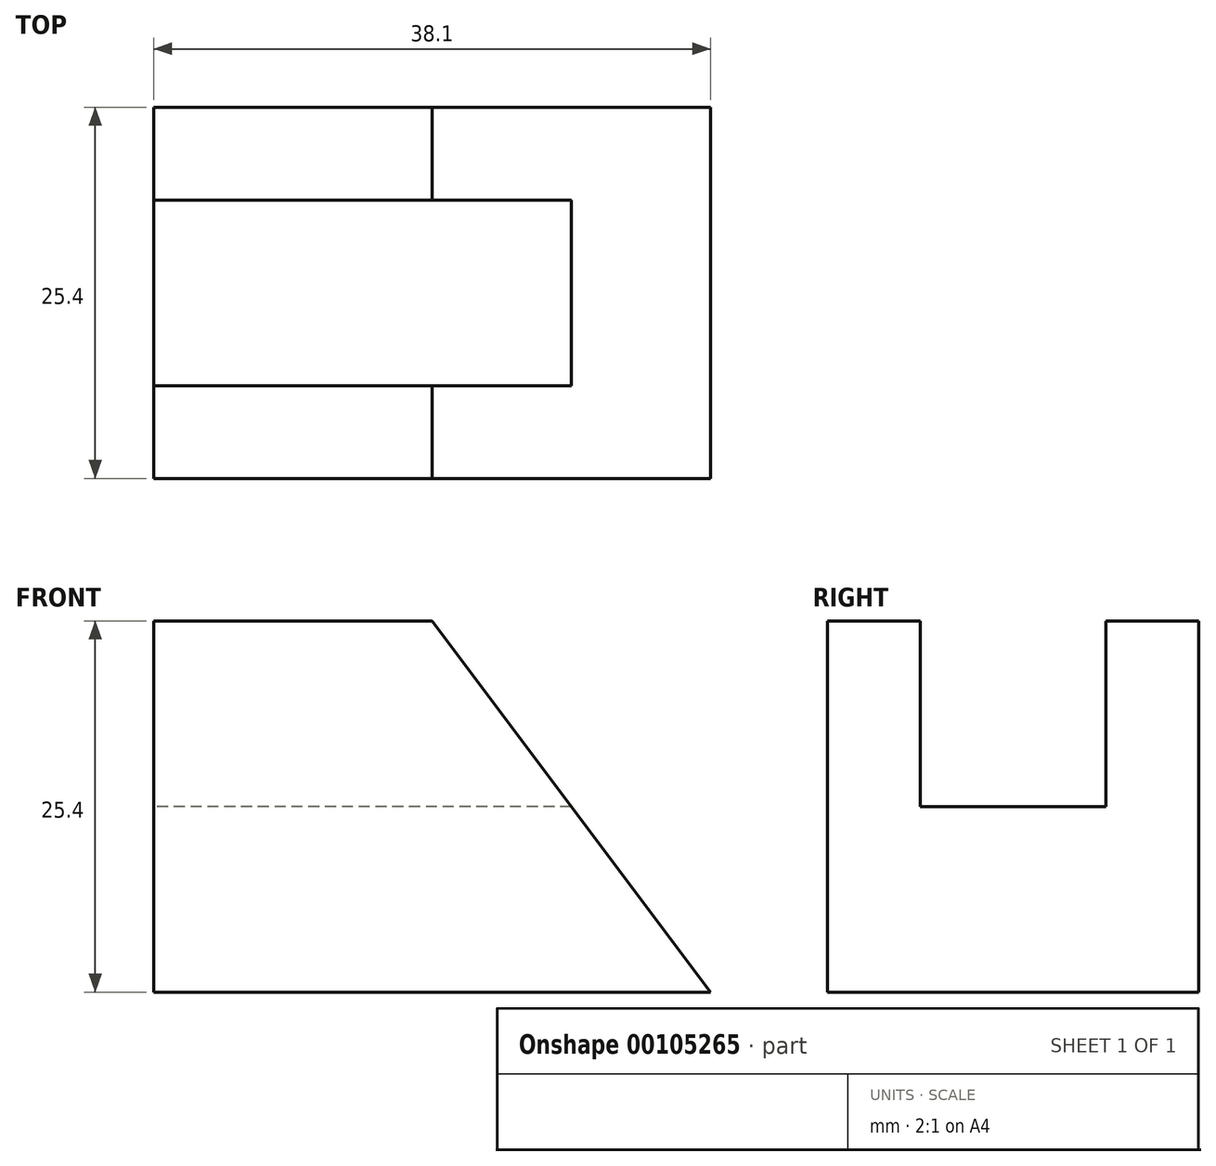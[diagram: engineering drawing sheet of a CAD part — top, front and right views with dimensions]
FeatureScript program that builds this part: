
annotation { "Feature Type Name" : "Feature", "Feature Type Description" : "" }
export const myFeature = defineFeature(function(context is Context, id is Id, definition is map)
    precondition{}
    {
        {
            var Q0;
            Q0=qCreatedBy(makeId("Front.planeOp"),FACE);
            var sketch = newSketch(context, id + "F0", { "sketchPlane" : qUnion([Q0])});
            skLineSegment(sketch, "E0.top", {"start": v(0, 25.4) * mm, "end": v(19.05, 25.4) * mm});
            skLineSegment(sketch, "E0.left", {"start": v(0, 0) * mm, "end": v(0, 25.4) * mm});
            skLineSegment(sketch, "E1", {"start": v(19.05, 25.4) * mm, "end": v(38.1, 0) * mm});
            skLineSegment(sketch, "E2", {"start": v(0, 0) * mm, "end": v(38.1, 0) * mm});
            skSolve(sketch);
        }
        {
            var Q0;
            Q0=makeQuery(id+"F0.imprint","IMPRINT",FACE,{"disambiguationData":[TD([[makeQuery(id+"F0.imprint","IMPRINT",EDGE,{"derivedFrom":sQuery(id+"F0.wireOp",EDGE,"E0.top")}),-1.0]])]});
            extrude(context, id + "F1", {"entities" : qUnion([Q0]), "depth" : 25.4 * mm});
        }
        {
            var Q0;
            Q0=makeQuery(id+"F1.opExtrude","SWEPT_FACE",FACE,{"disambiguationData":[OSD([sQuery(id+"F0.wireOp",EDGE,"E0.left")])]});
            var sketch = newSketch(context, id + "F2", { "sketchPlane" : qUnion([Q0])});
            skLineSegment(sketch, "E3.bottom", {"start": v(6.35, 25.4) * mm, "end": v(19.05, 25.4) * mm});
            skLineSegment(sketch, "E3.top", {"start": v(6.35, 12.7) * mm, "end": v(19.05, 12.7) * mm});
            skLineSegment(sketch, "E3.left", {"start": v(6.35, 25.4) * mm, "end": v(6.35, 12.7) * mm});
            skLineSegment(sketch, "E3.right", {"start": v(19.05, 25.4) * mm, "end": v(19.05, 12.7) * mm});
            skSolve(sketch);
        }
        {
            var Q0;
            Q0=makeQuery(id+"F2.imprint","IMPRINT",FACE,{"disambiguationData":[TD([[makeQuery(id+"F2.imprint","IMPRINT",EDGE,{"derivedFrom":sQuery(id+"F2.wireOp",EDGE,"E3.bottom")}),1.0]])]});
            extrude(context, id + "F3", {"entities" : qUnion([Q0]), "operationType" : NewBodyOperationType.REMOVE, "endBound" : BoundingType.THROUGH_ALL, "oppositeDirection" : true, "depth" : 25.4 * mm});
        }
    });
